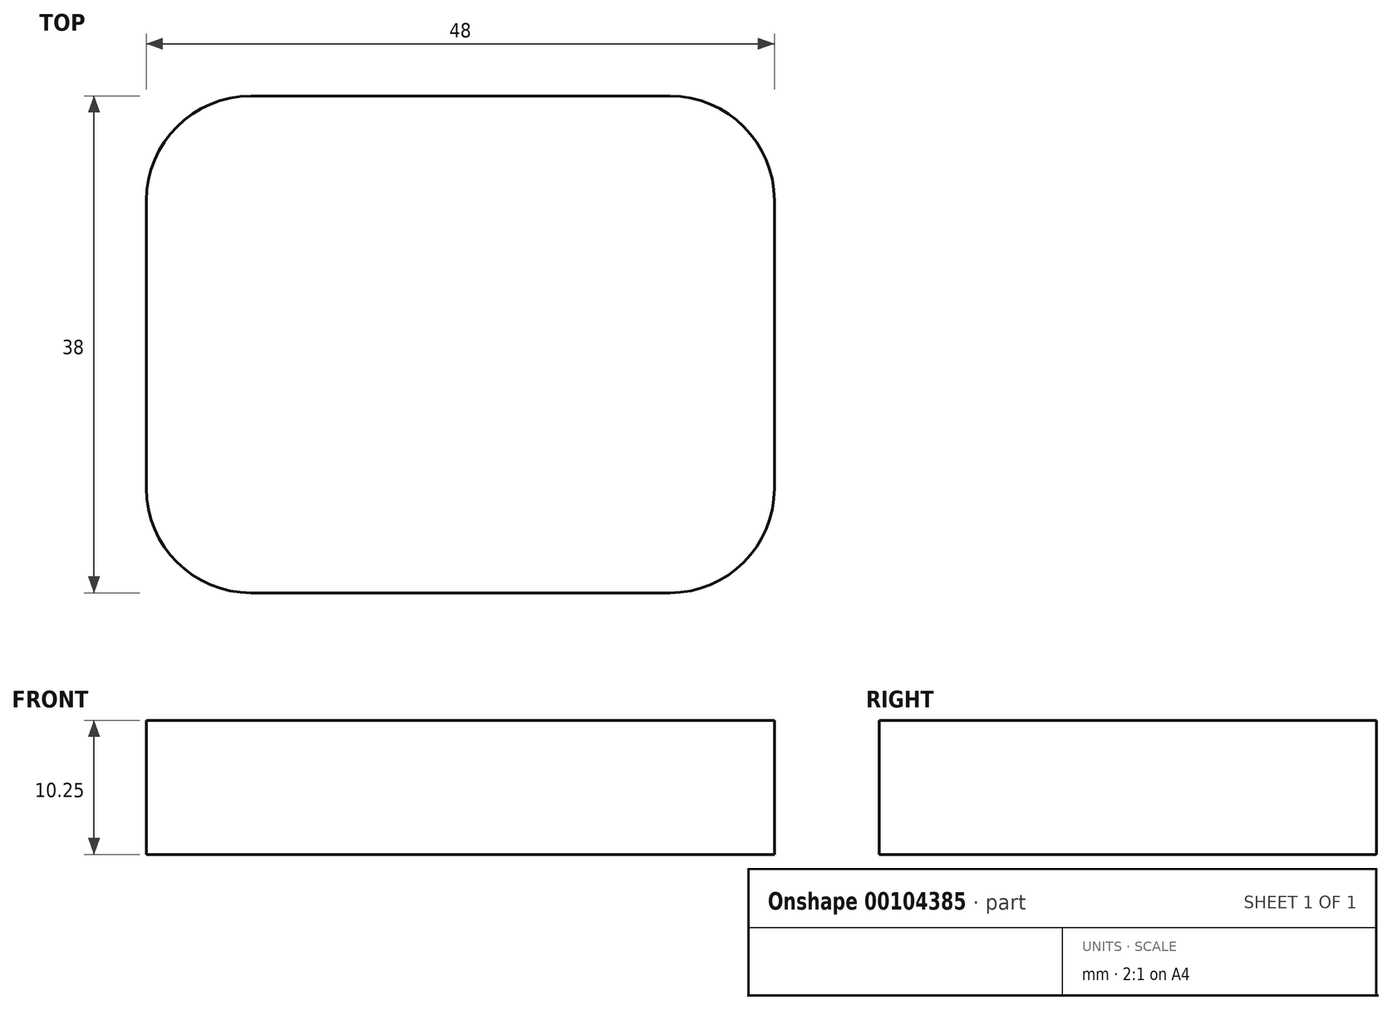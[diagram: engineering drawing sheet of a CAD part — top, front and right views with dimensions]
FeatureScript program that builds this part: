
annotation { "Feature Type Name" : "Feature", "Feature Type Description" : "" }
export const myFeature = defineFeature(function(context is Context, id is Id, definition is map)
    precondition{}
    {
        {
            var Q0;
            Q0=qCreatedBy(makeId("Top.planeOp"),FACE);
            var sketch = newSketch(context, id + "F0", { "sketchPlane" : qUnion([Q0])});
            skLineSegment(sketch, "E0.bottom", {"start": v(-16, 19) * mm, "end": v(16, 19) * mm});
            skLineSegment(sketch, "E0.top", {"start": v(-16, -19) * mm, "end": v(16, -19) * mm});
            skLineSegment(sketch, "E0.left", {"start": v(-24, 11) * mm, "end": v(-24, -11) * mm});
            skLineSegment(sketch, "E0.right", {"start": v(24, 11) * mm, "end": v(24, -11) * mm});
            skPoint(sketch, "E1.visualSharp", {"position": v(24, 19) * mm});
            skArc(sketch, "E1.filletArc", {"start": v(24, 11) * mm, "mid": v(21.66, 16.66) * mm, "end": v(16, 19) * mm});
            skPoint(sketch, "E2.visualSharp", {"position": v(24, -19) * mm});
            skArc(sketch, "E2.filletArc", {"start": v(16, -19) * mm, "mid": v(21.66, -16.66) * mm, "end": v(24, -11) * mm});
            skPoint(sketch, "E3.visualSharp", {"position": v(-24, -19) * mm});
            skArc(sketch, "E3.filletArc", {"start": v(-24, -11) * mm, "mid": v(-21.66, -16.66) * mm, "end": v(-16, -19) * mm});
            skPoint(sketch, "E4.visualSharp", {"position": v(-24, 19) * mm});
            skArc(sketch, "E4.filletArc", {"start": v(-16, 19) * mm, "mid": v(-21.66, 16.66) * mm, "end": v(-24, 11) * mm});
            skLineSegment(sketch, "E5.bottom", {"start": v(16.1, -22.18) * mm, "end": v(-8.9, -22.18) * mm});
            skLineSegment(sketch, "E5.top", {"start": v(16.1, 21.52) * mm, "end": v(-8.9, 21.52) * mm});
            skLineSegment(sketch, "E5.left", {"start": v(24.1, -14.18) * mm, "end": v(24.1, 13.52) * mm});
            skLineSegment(sketch, "E5.right", {"start": v(-8.9, -22.18) * mm, "end": v(-8.9, 21.52) * mm});
            skPoint(sketch, "E6.visualSharp", {"position": v(24.1, -22.18) * mm});
            skArc(sketch, "E6.filletArc", {"start": v(16.1, -22.18) * mm, "mid": v(21.75, -19.83) * mm, "end": v(24.1, -14.18) * mm});
            skPoint(sketch, "E7.visualSharp", {"position": v(24.1, 21.52) * mm});
            skArc(sketch, "E7.filletArc", {"start": v(24.1, 13.52) * mm, "mid": v(21.75, 19.18) * mm, "end": v(16.1, 21.52) * mm});
            skSolve(sketch);
        }
        {
            var Q0;
            Q0=makeQuery(id+"F0.imprint","IMPRINT",FACE,{"disambiguationData":[TD([[makeQuery(id+"F0.imprint","IMPRINT",EDGE,{"derivedFrom":sQuery(id+"F0.wireOp",EDGE,"E0.bottom")}),-1.0]])]});
            extrude(context, id + "F1", {"entities" : qUnion([Q0]), "depth" : 10.25 * mm});
        }
    });
